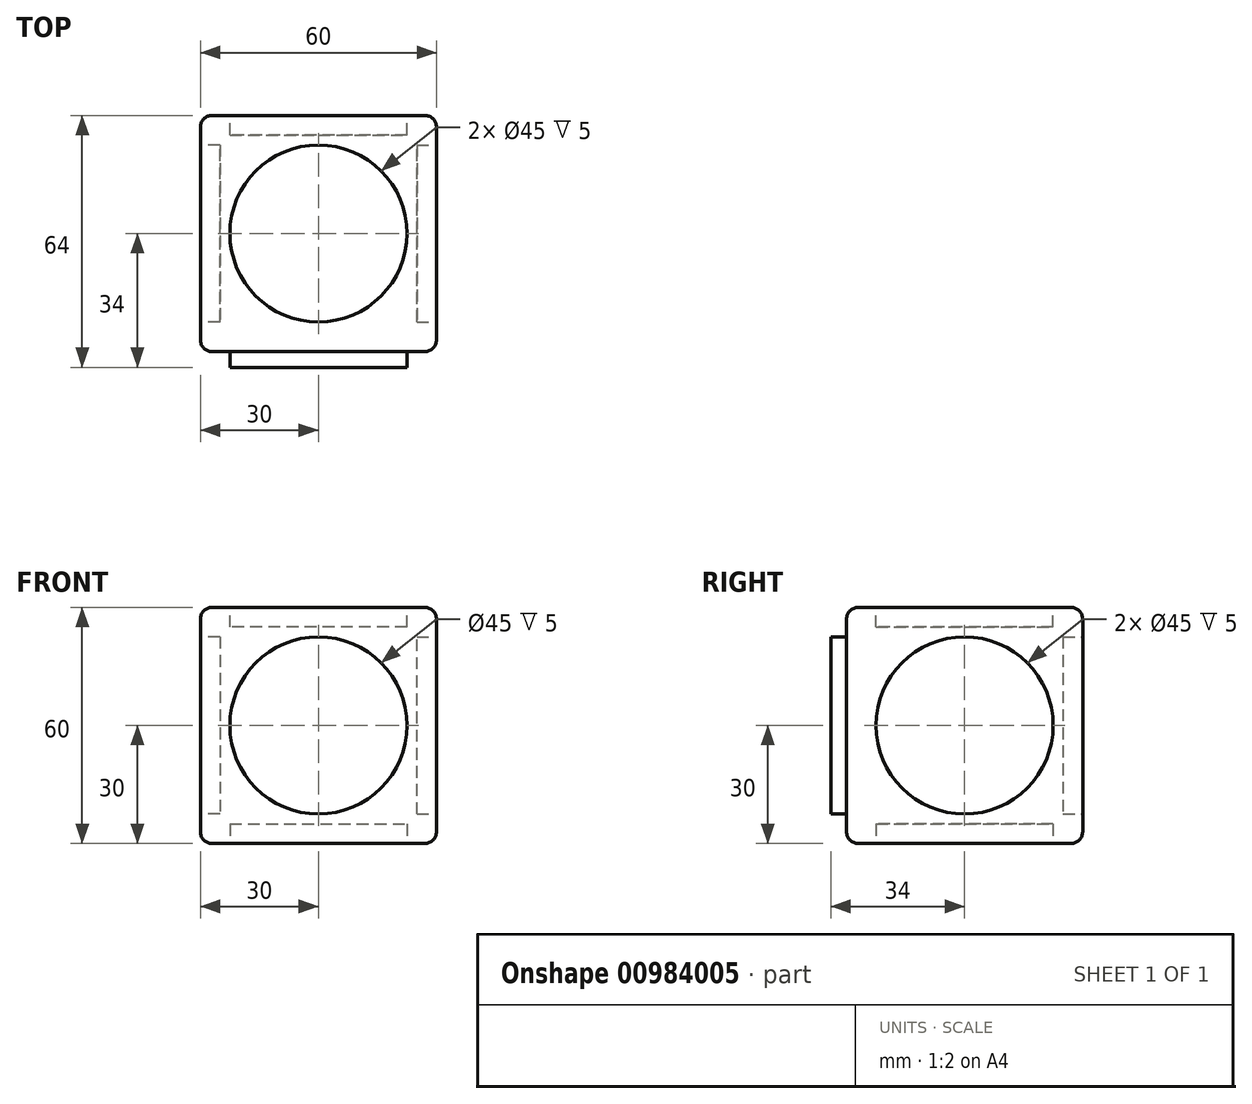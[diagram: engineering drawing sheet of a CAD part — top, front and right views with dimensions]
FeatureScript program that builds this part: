
annotation { "Feature Type Name" : "Feature", "Feature Type Description" : "" }
export const myFeature = defineFeature(function(context is Context, id is Id, definition is map)
    precondition{}
    {
        {
            var Q0;
            Q0=qCreatedBy(makeId("Top.planeOp"),FACE);
            var sketch = newSketch(context, id + "F0", { "sketchPlane" : qUnion([Q0])});
            skLineSegment(sketch, "E0.bottom", {"start": v(0, 0) * mm, "end": v(60, 0) * mm});
            skLineSegment(sketch, "E0.top", {"start": v(0, 60) * mm, "end": v(60, 60) * mm});
            skLineSegment(sketch, "E0.left", {"start": v(0, 0) * mm, "end": v(0, 60) * mm});
            skLineSegment(sketch, "E0.right", {"start": v(60, 0) * mm, "end": v(60, 60) * mm});
            skSolve(sketch);
        }
        {
            var Q0;
            Q0=makeQuery(id+"F0.imprint","IMPRINT",FACE,{"disambiguationData":[TD([[makeQuery(id+"F0.imprint","IMPRINT",EDGE,{"derivedFrom":sQuery(id+"F0.wireOp",EDGE,"E0.bottom")}),1.0]])]});
            extrude(context, id + "F1", {"entities" : qUnion([Q0]), "depth" : 60 * mm, "offsetDistance" : 25 * mm});
        }
        {
            var Q0;
            Q0=makeQuery(id+"F1.opExtrude","CAP_FACE",FACE,{"disambiguationData":[OSD([sQuery(id+"F0.wireOp",EDGE,"E0.bottom"),sQuery(id+"F0.wireOp",EDGE,"E0.top"),sQuery(id+"F0.wireOp",EDGE,"E0.left"),sQuery(id+"F0.wireOp",EDGE,"E0.right")])],"isStart":false});
            var Q1;
            Q1=makeQuery(id+"F1.opExtrude","SWEPT_FACE",FACE,{"disambiguationData":[OSD([sQuery(id+"F0.wireOp",EDGE,"E0.left")])]});
            var Q2;
            Q2=makeQuery(id+"F1.opExtrude","SWEPT_FACE",FACE,{"disambiguationData":[OSD([sQuery(id+"F0.wireOp",EDGE,"E0.top")])]});
            var Q3;
            Q3=makeQuery(id+"F1.opExtrude","SWEPT_FACE",FACE,{"disambiguationData":[OSD([sQuery(id+"F0.wireOp",EDGE,"E0.right")])]});
            var Q4;
            Q4=makeQuery(id+"F1.opExtrude","SWEPT_FACE",FACE,{"disambiguationData":[OSD([sQuery(id+"F0.wireOp",EDGE,"E0.bottom")])]});
            fillet(context, id + "F2", {"entities" : qUnion([Q0, Q1, Q2, Q3, Q4]), "radius" : 3 * mm, "tangentPropagation" : true, "allowEdgeOverflow" : false});
        }
        {
            var Q0;
            Q0=makeQuery(id+"F1.opExtrude","CAP_FACE",FACE,{"disambiguationData":[OSD([sQuery(id+"F0.wireOp",EDGE,"E0.bottom"),sQuery(id+"F0.wireOp",EDGE,"E0.top"),sQuery(id+"F0.wireOp",EDGE,"E0.left"),sQuery(id+"F0.wireOp",EDGE,"E0.right")])],"isStart":false});
            var sketch = newSketch(context, id + "F3", { "sketchPlane" : qUnion([Q0])});
            skLineSegment(sketch, "E1", {"start": v(3, 57) * mm, "end": v(57, 3) * mm});
            skCircle(sketch, "E2", {"center": v(30, 30) * mm, "radius": 22.5 * mm});
            skSolve(sketch);
        }
        {
            var Q0;
            Q0 = qSketchRegion(id + "F3", true);
            extrude(context, id + "F4", {"entities" : qUnion([Q0]), "operationType" : NewBodyOperationType.REMOVE, "oppositeDirection" : true, "depth" : 5 * mm, "offsetDistance" : 25 * mm});
        }
        {
            var Q0;
            Q0=makeQuery(id+"F1.opExtrude","SWEPT_FACE",FACE,{"disambiguationData":[OSD([sQuery(id+"F0.wireOp",EDGE,"E0.right")])]});
            var sketch = newSketch(context, id + "F5", { "sketchPlane" : qUnion([Q0])});
            skCircle(sketch, "E3", {"center": v(30, 30) * mm, "radius": 22.5 * mm});
            skSolve(sketch);
        }
        {
            var Q0;
            Q0=makeQuery(id+"F5.imprint","IMPRINT",FACE,{"disambiguationData":[TD([[makeQuery(id+"F5.imprint","IMPRINT",EDGE,{"derivedFrom":sQuery(id+"F5.wireOp",EDGE,"E3")}),1.0]])]});
            extrude(context, id + "F6", {"entities" : qUnion([Q0]), "operationType" : NewBodyOperationType.REMOVE, "oppositeDirection" : true, "depth" : 5 * mm, "offsetDistance" : 25 * mm});
        }
        {
            var Q0;
            Q0=makeQuery(id+"F1.opExtrude","SWEPT_FACE",FACE,{"disambiguationData":[OSD([sQuery(id+"F0.wireOp",EDGE,"E0.bottom")])]});
            var sketch = newSketch(context, id + "F7", { "sketchPlane" : qUnion([Q0])});
            skCircle(sketch, "E4", {"center": v(30, 30) * mm, "radius": 22.5 * mm});
            skSolve(sketch);
        }
        {
            var Q0;
            Q0=makeQuery(id+"F7.imprint","IMPRINT",FACE,{"disambiguationData":[TD([[makeQuery(id+"F7.imprint","IMPRINT",EDGE,{"derivedFrom":sQuery(id+"F7.wireOp",EDGE,"E4")}),1.0]])]});
            extrude(context, id + "F8", {"entities" : qUnion([Q0]), "operationType" : NewBodyOperationType.ADD, "depth" : 4 * mm, "offsetDistance" : 25 * mm});
        }
        {
            var Q0;
            Q0=makeQuery(id+"F1.opExtrude","SWEPT_FACE",FACE,{"disambiguationData":[OSD([sQuery(id+"F0.wireOp",EDGE,"E0.top")])]});
            var sketch = newSketch(context, id + "F9", { "sketchPlane" : qUnion([Q0])});
            skCircle(sketch, "E5", {"center": v(-30, 30) * mm, "radius": 22.5 * mm});
            skSolve(sketch);
        }
        {
            var Q0;
            Q0=makeQuery(id+"F9.imprint","IMPRINT",FACE,{"disambiguationData":[TD([[makeQuery(id+"F9.imprint","IMPRINT",EDGE,{"derivedFrom":sQuery(id+"F9.wireOp",EDGE,"E5")}),1.0]])]});
            extrude(context, id + "F10", {"entities" : qUnion([Q0]), "operationType" : NewBodyOperationType.REMOVE, "oppositeDirection" : true, "depth" : 5 * mm, "offsetDistance" : 25 * mm});
        }
        {
            var Q0;
            Q0=makeQuery(id+"F1.opExtrude","SWEPT_FACE",FACE,{"disambiguationData":[OSD([sQuery(id+"F0.wireOp",EDGE,"E0.left")])]});
            var sketch = newSketch(context, id + "F11", { "sketchPlane" : qUnion([Q0])});
            skCircle(sketch, "E6", {"center": v(-30, 30) * mm, "radius": 22.5 * mm});
            skSolve(sketch);
        }
        {
            var Q0;
            Q0=makeQuery(id+"F11.imprint","IMPRINT",FACE,{"disambiguationData":[TD([[makeQuery(id+"F11.imprint","IMPRINT",EDGE,{"derivedFrom":sQuery(id+"F11.wireOp",EDGE,"E6")}),1.0]])]});
            extrude(context, id + "F12", {"entities" : qUnion([Q0]), "operationType" : NewBodyOperationType.REMOVE, "oppositeDirection" : true, "depth" : 5 * mm, "offsetDistance" : 25 * mm});
        }
        {
            var Q0;
            Q0=makeQuery(id+"F1.opExtrude","CAP_FACE",FACE,{"disambiguationData":[OSD([sQuery(id+"F0.wireOp",EDGE,"E0.bottom"),sQuery(id+"F0.wireOp",EDGE,"E0.top"),sQuery(id+"F0.wireOp",EDGE,"E0.left"),sQuery(id+"F0.wireOp",EDGE,"E0.right")])],"isStart":true});
            var sketch = newSketch(context, id + "F13", { "sketchPlane" : qUnion([Q0])});
            skCircle(sketch, "E7", {"center": v(30, -30) * mm, "radius": 22.5 * mm});
            skSolve(sketch);
        }
        {
            var Q0;
            Q0=makeQuery(id+"F13.imprint","IMPRINT",FACE,{"disambiguationData":[TD([[makeQuery(id+"F13.imprint","IMPRINT",EDGE,{"derivedFrom":sQuery(id+"F13.wireOp",EDGE,"E7")}),1.0]])]});
            extrude(context, id + "F14", {"entities" : qUnion([Q0]), "operationType" : NewBodyOperationType.REMOVE, "oppositeDirection" : true, "depth" : 5 * mm, "offsetDistance" : 25 * mm});
        }
    });
